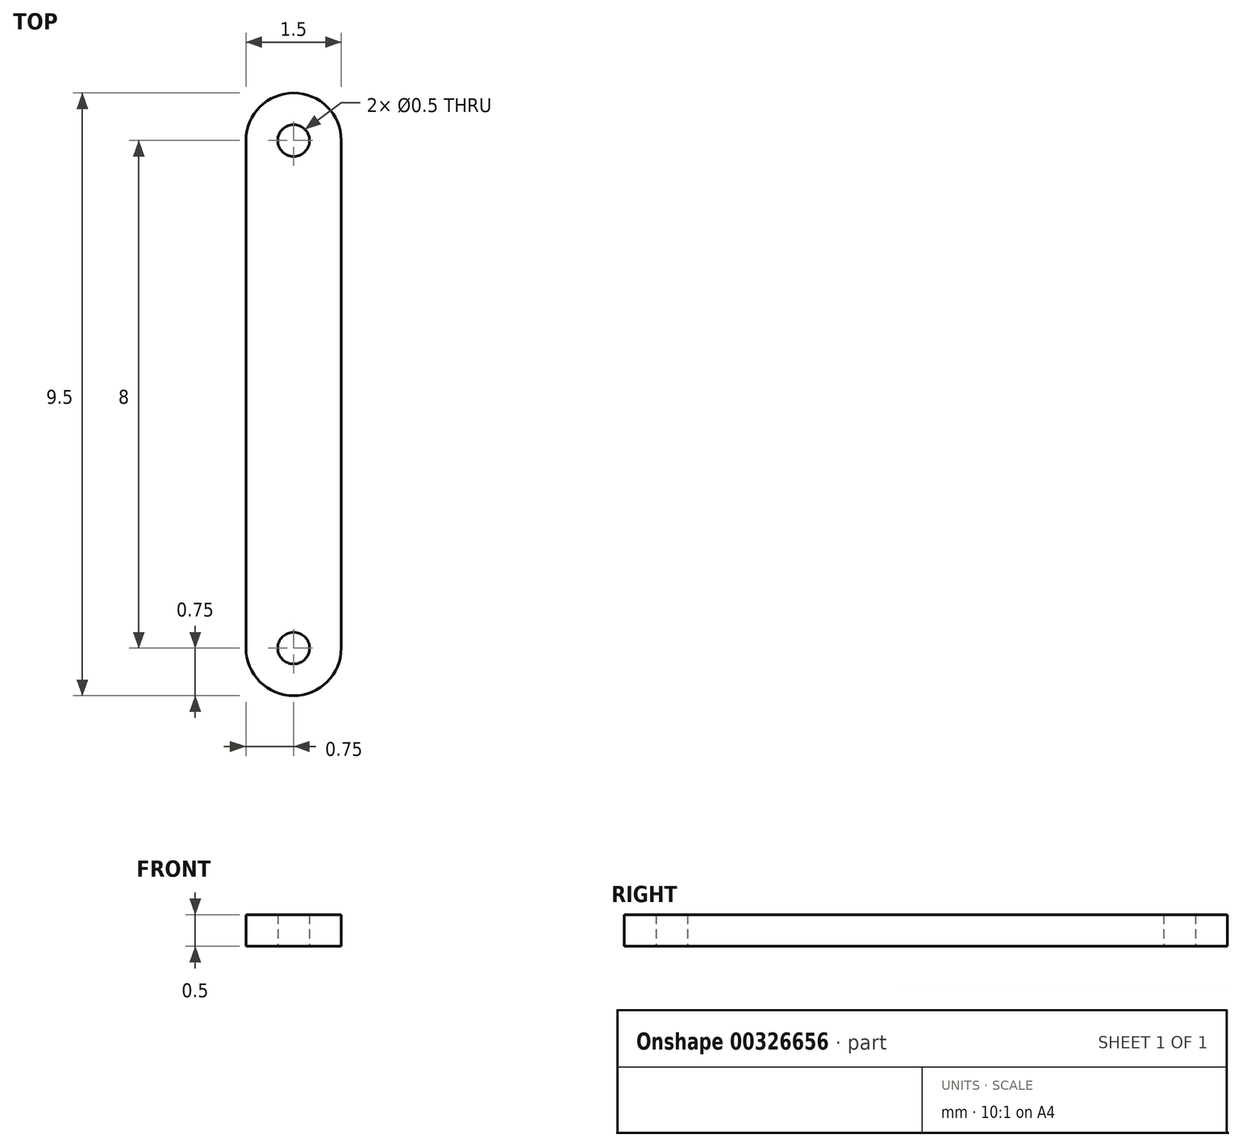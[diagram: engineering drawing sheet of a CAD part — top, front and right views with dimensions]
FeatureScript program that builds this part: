
annotation { "Feature Type Name" : "Feature", "Feature Type Description" : "" }
export const myFeature = defineFeature(function(context is Context, id is Id, definition is map)
    precondition{}
    {
        {
            var Q0;
            Q0=qCreatedBy(makeId("Top.planeOp"),FACE);
            var sketch = newSketch(context, id + "F0", { "sketchPlane" : qUnion([Q0])});
            skLineSegment(sketch, "E0.bottom", {"start": v(0, 4.75) * mm, "end": v(0, 4.75) * mm});
            skLineSegment(sketch, "E0.top", {"start": v(0, -4.75) * mm, "end": v(0, -4.75) * mm});
            skLineSegment(sketch, "E0.left", {"start": v(0.75, 4) * mm, "end": v(0.75, -4) * mm});
            skLineSegment(sketch, "E0.right", {"start": v(-0.75, 4) * mm, "end": v(-0.75, -4) * mm});
            skPoint(sketch, "E0.middle", {"position": v(0, 0) * mm});
            skPoint(sketch, "E1.visualSharp", {"position": v(0.75, 4.75) * mm});
            skArc(sketch, "E1.filletArc", {"start": v(0.75, 4) * mm, "mid": v(0.53, 4.53) * mm, "end": v(0, 4.75) * mm});
            skPoint(sketch, "E2.visualSharp", {"position": v(-0.75, 4.75) * mm});
            skArc(sketch, "E2.filletArc", {"start": v(0, 4.75) * mm, "mid": v(-0.53, 4.53) * mm, "end": v(-0.75, 4) * mm});
            skPoint(sketch, "E3.visualSharp", {"position": v(0.75, -4.75) * mm});
            skArc(sketch, "E3.filletArc", {"start": v(0, -4.75) * mm, "mid": v(0.53, -4.53) * mm, "end": v(0.75, -4) * mm});
            skPoint(sketch, "E4.visualSharp", {"position": v(-0.75, -4.75) * mm});
            skArc(sketch, "E4.filletArc", {"start": v(-0.75, -4) * mm, "mid": v(-0.53, -4.53) * mm, "end": v(0, -4.75) * mm});
            skCircle(sketch, "E5", {"center": v(0, 4) * mm, "radius": 0.25 * mm});
            skCircle(sketch, "E6", {"center": v(0, -4) * mm, "radius": 0.25 * mm});
            skSolve(sketch);
        }
        {
            var Q0;
            Q0=makeQuery(id+"F0.imprint","IMPRINT",FACE,{"disambiguationData":[TD([[makeQuery(id+"F0.imprint","IMPRINT",EDGE,{"derivedFrom":sQuery(id+"F0.wireOp",EDGE,"E0.left")}),-1.0]])]});
            extrude(context, id + "F1", {"entities" : qUnion([Q0]), "depth" : 0.5 * mm});
        }
    });
